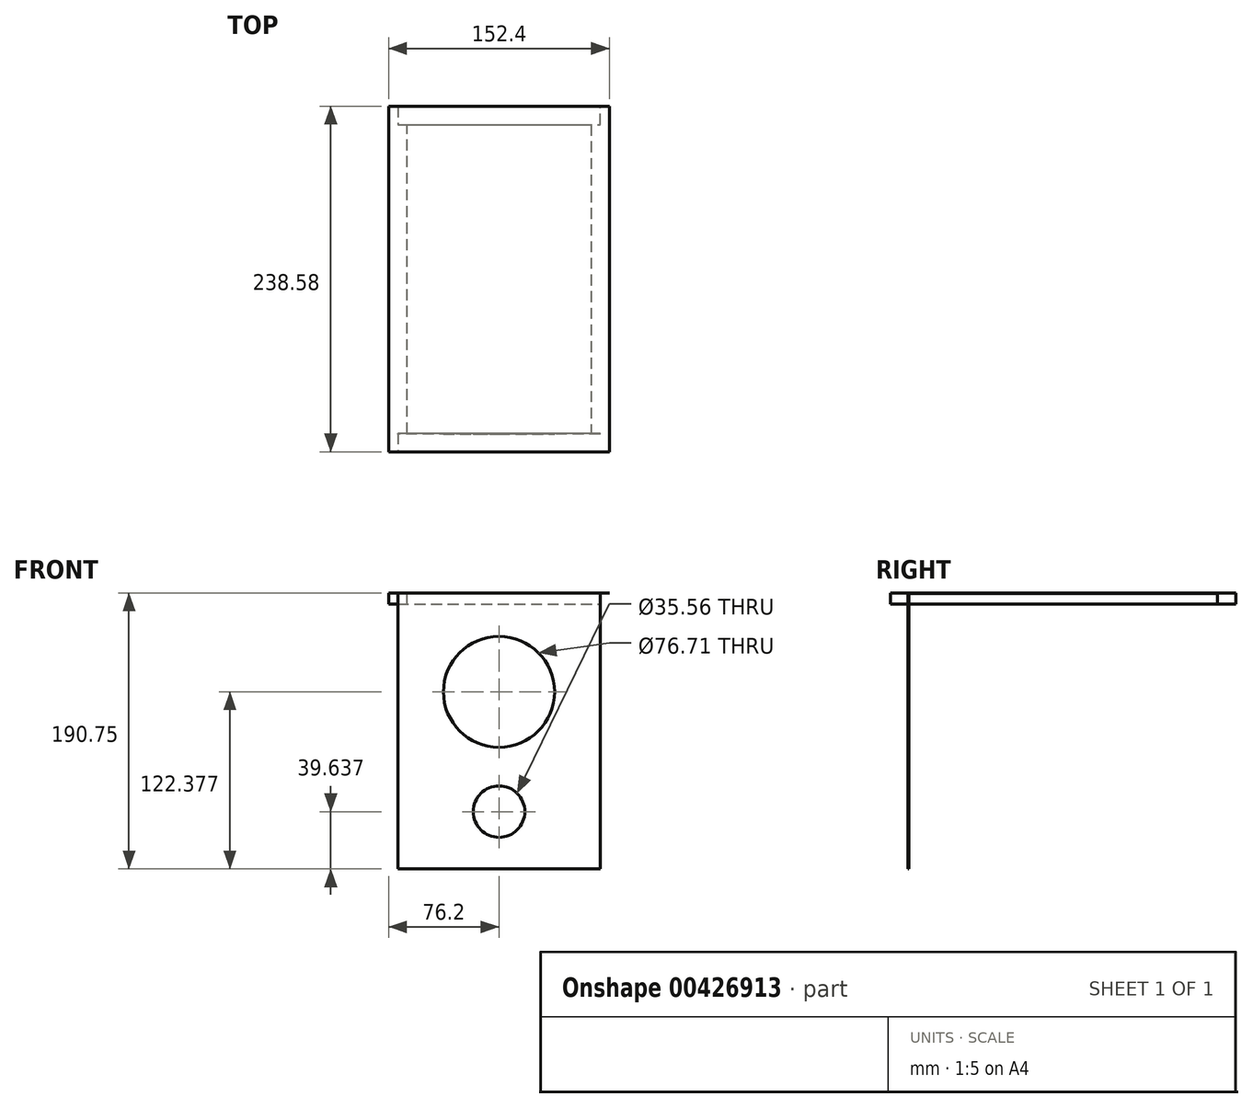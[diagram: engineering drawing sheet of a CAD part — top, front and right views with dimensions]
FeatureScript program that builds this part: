
annotation { "Feature Type Name" : "Feature", "Feature Type Description" : "" }
export const myFeature = defineFeature(function(context is Context, id is Id, definition is map)
    precondition{}
    {
        {
            assignVariable(context, id + "F0", {"name" : "interiorHeight", "anyValue" : 7});
        }
        {
            assignVariable(context, id + "F1", {"name" : "t", "anyValue" : 0.5});
        }
        {
            var Q0;
            Q0=qCreatedBy(makeId("Front.planeOp"),FACE);
            var sketch = newSketch(context, id + "F2", { "sketchPlane" : qUnion([Q0])});
            skLineSegment(sketch, "E0.bottom", {"start": v(69.85, -95.25) * mm, "end": v(-69.85, -95.25) * mm});
            skLineSegment(sketch, "E0.top", {"start": v(69.85, 95.25) * mm, "end": v(-69.85, 95.25) * mm});
            skLineSegment(sketch, "E0.left", {"start": v(69.85, -95.25) * mm, "end": v(69.85, 95.25) * mm});
            skLineSegment(sketch, "E0.right", {"start": v(-69.85, -95.25) * mm, "end": v(-69.85, 95.25) * mm});
            skPoint(sketch, "E0.middle", {"position": v(0, 0) * mm});
            skSolve(sketch);
        }
        {
            var Q0;
            Q0 = qSketchRegion(id + "F2", true);
            extrude(context, id + "F3", {"entities" : qUnion([Q0]), "depth" : (getVariable(context, 't')) * mm});
        }
        {
            var Q0;
            Q0=makeQuery(id+"F3.opExtrude","CAP_FACE",FACE,{"disambiguationData":[OSD([sQuery(id+"F2.wireOp",EDGE,"E0.bottom"),sQuery(id+"F2.wireOp",EDGE,"E0.top"),sQuery(id+"F2.wireOp",EDGE,"E0.left"),sQuery(id+"F2.wireOp",EDGE,"E0.right")])],"isStart":false});
            var sketch = newSketch(context, id + "F4", { "sketchPlane" : qUnion([Q0])});
            skCircle(sketch, "E1", {"center": v(0, -55.61) * mm, "radius": 17.78 * mm});
            skSolve(sketch);
        }
        {
            var Q0;
            Q0 = qSketchRegion(id + "F4", true);
            extrude(context, id + "F5", {"entities" : qUnion([Q0]), "operationType" : NewBodyOperationType.REMOVE, "oppositeDirection" : true, "depth" : (getVariable(context, 't')) * mm});
        }
        {
            var Q0;
            Q0=makeQuery(id+"F3.opExtrude","CAP_FACE",FACE,{"disambiguationData":[OSD([sQuery(id+"F2.wireOp",EDGE,"E0.bottom"),sQuery(id+"F2.wireOp",EDGE,"E0.top"),sQuery(id+"F2.wireOp",EDGE,"E0.left"),sQuery(id+"F2.wireOp",EDGE,"E0.right")])],"isStart":false});
            var sketch = newSketch(context, id + "F6", { "sketchPlane" : qUnion([Q0])});
            skCircle(sketch, "E2", {"center": v(0, 27.13) * mm, "radius": 38.35 * mm});
            skSolve(sketch);
        }
        {
            var Q0;
            Q0 = qSketchRegion(id + "F6", true);
            extrude(context, id + "F7", {"entities" : qUnion([Q0]), "operationType" : NewBodyOperationType.REMOVE, "oppositeDirection" : true, "depth" : (getVariable(context, 't')) * mm});
        }
        {
            var Q0;
            Q0=qCreatedBy(makeId("Right.planeOp"),FACE);
            var sketch = newSketch(context, id + "F8", { "sketchPlane" : qUnion([Q0])});
            skLineSegment(sketch, "E3.bottom", {"start": v(-119.3, -95.25) * mm, "end": v(119.3, -95.25) * mm});
            skLineSegment(sketch, "E3.top", {"start": v(-119.3, 95.25) * mm, "end": v(119.3, 95.25) * mm});
            skLineSegment(sketch, "E3.left", {"start": v(-119.3, -95.25) * mm, "end": v(-119.3, 95.25) * mm});
            skLineSegment(sketch, "E3.right", {"start": v(119.3, -95.25) * mm, "end": v(119.3, 95.25) * mm});
            skPoint(sketch, "E3.middle", {"position": v(0, 0) * mm});
            skSolve(sketch);
        }
        {
            var Q0;
            Q0 = qSketchRegion(id + "F8", true);
            extrude(context, id + "F9", {"entities" : qUnion([Q0]), "oppositeDirection" : true, "depth" : (getVariable(context, 't')) * mm});
        }
        {
            var Q0;
            Q0=makeQuery(id+"F9.opExtrude","CAP_FACE",FACE,{"disambiguationData":[OSD([sQuery(id+"F8.wireOp",EDGE,"E3.bottom"),sQuery(id+"F8.wireOp",EDGE,"E3.top"),sQuery(id+"F8.wireOp",EDGE,"E3.left"),sQuery(id+"F8.wireOp",EDGE,"E3.right")])],"isStart":true});
            var sketch = newSketch(context, id + "F10", { "sketchPlane" : qUnion([Q0])});
            skLineSegment(sketch, "E4.bottom", {"start": v(-119.3, 95.25) * mm, "end": v(-106.6, 95.25) * mm});
            skLineSegment(sketch, "E4.top", {"start": v(-119.3, -95.25) * mm, "end": v(-106.6, -95.25) * mm});
            skLineSegment(sketch, "E4.left", {"start": v(-119.3, 95.25) * mm, "end": v(-119.3, -95.25) * mm});
            skLineSegment(sketch, "E4.right", {"start": v(-106.6, 95.25) * mm, "end": v(-106.6, -95.25) * mm});
            skSolve(sketch);
        }
        {
            var Q0;
            Q0 = qSketchRegion(id + "F10", true);
            extrude(context, id + "F11", {"entities" : qUnion([Q0]), "operationType" : NewBodyOperationType.REMOVE, "oppositeDirection" : true, "depth" : (getVariable(context, 't') / 2) * mm});
        }
        {
            var Q0;
            Q0=makeQuery(id+"F9.opExtrude","CAP_FACE",FACE,{"disambiguationData":[OSD([sQuery(id+"F8.wireOp",EDGE,"E3.bottom"),sQuery(id+"F8.wireOp",EDGE,"E3.top"),sQuery(id+"F8.wireOp",EDGE,"E3.left"),sQuery(id+"F8.wireOp",EDGE,"E3.right")])],"isStart":true});
            var sketch = newSketch(context, id + "F12", { "sketchPlane" : qUnion([Q0])});
            skLineSegment(sketch, "E5.bottom", {"start": v(119.3, 95.25) * mm, "end": v(106.6, 95.25) * mm});
            skLineSegment(sketch, "E5.top", {"start": v(119.3, -95.25) * mm, "end": v(106.6, -95.25) * mm});
            skLineSegment(sketch, "E5.left", {"start": v(119.3, 95.25) * mm, "end": v(119.3, -95.25) * mm});
            skLineSegment(sketch, "E5.right", {"start": v(106.6, 95.25) * mm, "end": v(106.6, -95.25) * mm});
            skSolve(sketch);
        }
        {
            var Q0;
            Q0 = qSketchRegion(id + "F12", true);
            extrude(context, id + "F13", {"entities" : qUnion([Q0]), "operationType" : NewBodyOperationType.REMOVE, "oppositeDirection" : true, "depth" : (getVariable(context, 't') / 2) * mm});
        }
        {
            var Q0;
            Q0=makeQuery(id+"F3.opExtrude","SWEPT_FACE",FACE,{"disambiguationData":[OSD([sQuery(id+"F2.wireOp",EDGE,"E0.top")])]});
            var sketch = newSketch(context, id + "F14", { "sketchPlane" : qUnion([Q0])});
            skLineSegment(sketch, "E6", {"start": v(-69.85, -12.7) * mm, "end": v(-76.2, -12.7) * mm});
            skLineSegment(sketch, "E7", {"start": v(-76.2, -12.7) * mm, "end": v(-76.2, 225.88) * mm});
            skLineSegment(sketch, "E8", {"start": v(-76.2, 225.88) * mm, "end": v(-69.85, 225.88) * mm});
            skLineSegment(sketch, "E9", {"start": v(-69.85, 225.88) * mm, "end": v(-69.85, 213.18) * mm});
            skLineSegment(sketch, "E10", {"start": v(-69.85, 213.18) * mm, "end": v(-63.5, 213.18) * mm});
            skLineSegment(sketch, "E11", {"start": v(-63.5, 213.18) * mm, "end": v(-63.5, 0) * mm});
            skLineSegment(sketch, "E12", {"start": v(-63.5, 0) * mm, "end": v(-69.85, 0) * mm});
            skLineSegment(sketch, "E13", {"start": v(-69.85, 0) * mm, "end": v(-69.85, -12.7) * mm});
            skSolve(sketch);
        }
        {
            var Q0;
            Q0 = qSketchRegion(id + "F14", true);
            extrude(context, id + "F15", {"entities" : qUnion([Q0]), "oppositeDirection" : true, "depth" : (getVariable(context, 'interiorHeight') + getVariable(context, 't')) * mm});
        }
        {
            var Q0;
            Q0=makeQuery(id+"F9.opExtrude","SWEPT_BODY",BODY,{"disambiguationData":[OSD([sQuery(id+"F8.wireOp",EDGE,"E3.bottom"),sQuery(id+"F8.wireOp",EDGE,"E3.top"),sQuery(id+"F8.wireOp",EDGE,"E3.left"),sQuery(id+"F8.wireOp",EDGE,"E3.right")])]});
            deleteBodies(context, id + "F16", {"entities" : qUnion([Q0])});
        }
        {
            var Q0;
            Q0=makeQuery(id+"F15.opExtrude","CAP_FACE",FACE,{"disambiguationData":[OSD([sQuery(id+"F14.wireOp",EDGE,"E6"),sQuery(id+"F14.wireOp",EDGE,"E7"),sQuery(id+"F14.wireOp",EDGE,"E8"),sQuery(id+"F14.wireOp",EDGE,"E9"),sQuery(id+"F14.wireOp",EDGE,"E10"),sQuery(id+"F14.wireOp",EDGE,"E11"),sQuery(id+"F14.wireOp",EDGE,"E12"),sQuery(id+"F14.wireOp",EDGE,"E13")])],"isStart":true});
            var sketch = newSketch(context, id + "F17", { "sketchPlane" : qUnion([Q0])});
            skLineSegment(sketch, "E14.bottom", {"start": v(-69.85, 213.18) * mm, "end": v(69.85, 213.18) * mm});
            skLineSegment(sketch, "E14.top", {"start": v(-69.85, 225.88) * mm, "end": v(69.85, 225.88) * mm});
            skLineSegment(sketch, "E14.left", {"start": v(-69.85, 213.18) * mm, "end": v(-69.85, 225.88) * mm});
            skLineSegment(sketch, "E14.right", {"start": v(69.85, 213.18) * mm, "end": v(69.85, 225.88) * mm});
            skSolve(sketch);
        }
        {
            var Q0;
            Q0 = qSketchRegion(id + "F17", true);
            extrude(context, id + "F18", {"entities" : qUnion([Q0]), "oppositeDirection" : true, "depth" : (getVariable(context, 'interiorHeight') + getVariable(context, 't')) * mm});
        }
        {
            var Q0;
            Q0=makeQuery(id+"F15.opExtrude","CAP_FACE",FACE,{"disambiguationData":[OSD([sQuery(id+"F14.wireOp",EDGE,"E6"),sQuery(id+"F14.wireOp",EDGE,"E7"),sQuery(id+"F14.wireOp",EDGE,"E8"),sQuery(id+"F14.wireOp",EDGE,"E9"),sQuery(id+"F14.wireOp",EDGE,"E10"),sQuery(id+"F14.wireOp",EDGE,"E11"),sQuery(id+"F14.wireOp",EDGE,"E12"),sQuery(id+"F14.wireOp",EDGE,"E13")])],"isStart":true});
            var sketch = newSketch(context, id + "F19", { "sketchPlane" : qUnion([Q0])});
            skLineSegment(sketch, "E15.bottom", {"start": v(-76.2, -12.7) * mm, "end": v(76.2, -12.7) * mm});
            skLineSegment(sketch, "E15.top", {"start": v(-76.2, 225.88) * mm, "end": v(76.2, 225.88) * mm});
            skLineSegment(sketch, "E15.left", {"start": v(-76.2, -12.7) * mm, "end": v(-76.2, 225.88) * mm});
            skLineSegment(sketch, "E15.right", {"start": v(76.2, -12.7) * mm, "end": v(76.2, 225.88) * mm});
            skSolve(sketch);
        }
        {
            var Q0;
            Q0 = qSketchRegion(id + "F19", true);
            extrude(context, id + "F20", {"entities" : qUnion([Q0]), "depth" : (getVariable(context, 't') / 2) * mm});
        }
        {
            var Q0;
            Q0=makeQuery(id+"F20.opExtrude","CAP_FACE",FACE,{"disambiguationData":[OSD([sQuery(id+"F19.wireOp",EDGE,"E15.bottom"),sQuery(id+"F19.wireOp",EDGE,"E15.top"),sQuery(id+"F19.wireOp",EDGE,"E15.left"),sQuery(id+"F19.wireOp",EDGE,"E15.right")])],"isStart":true});
            var sketch = newSketch(context, id + "F21", { "sketchPlane" : qUnion([Q0])});
            skLineSegment(sketch, "E16.0", {"start": v(-63.5, -213.18) * mm, "end": v(63.5, -213.18) * mm});
            skLineSegment(sketch, "E16.1", {"start": v(-63.5, 0) * mm, "end": v(-63.5, -213.18) * mm});
            skLineSegment(sketch, "E16.2", {"start": v(63.5, 0) * mm, "end": v(-63.5, 0) * mm});
            skLineSegment(sketch, "E16.3", {"start": v(63.5, -213.18) * mm, "end": v(63.5, 0) * mm});
            skSolve(sketch);
        }
        {
            var Q0;
            Q0 = qSketchRegion(id + "F21", true);
            extrude(context, id + "F22", {"entities" : qUnion([Q0]), "depth" : (getVariable(context, 't') / 2) * mm});
        }
    });
